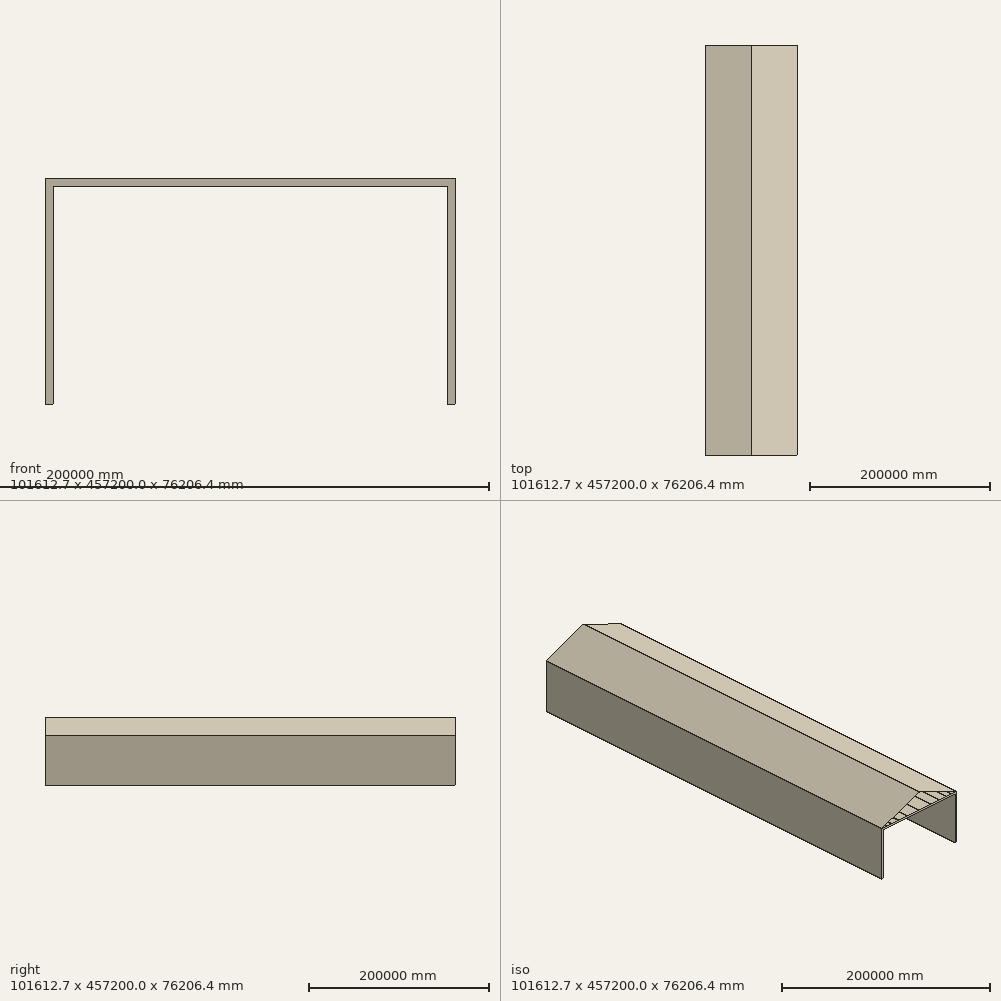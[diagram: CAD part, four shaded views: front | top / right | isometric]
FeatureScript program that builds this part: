
annotation { "Feature Type Name" : "Feature", "Feature Type Description" : "" }
export const myFeature = defineFeature(function(context is Context, id is Id, definition is map)
    precondition{}
    {
        {
            var Q0;
            Q0=qCreatedBy(makeId("Front.planeOp"),FACE);
            var sketch = newSketch(context, id + "F0", { "sketchPlane" : qUnion([Q0])});
            skLineSegment(sketch, "E0.bottom", {"start": v(0, 0) * mm, "end": v(2032, 0) * mm});
            skLineSegment(sketch, "E0.top", {"start": v(0, 55880) * mm, "end": v(101600, 55880) * mm});
            skLineSegment(sketch, "E0.left", {"start": v(0, 0) * mm, "end": v(0, 55880) * mm});
            skLineSegment(sketch, "E0.right", {"start": v(101600, 0) * mm, "end": v(101600, 55880) * mm});
            skLineSegment(sketch, "E1", {"start": v(0, 55880) * mm, "end": v(50800, 76200) * mm});
            skLineSegment(sketch, "E2", {"start": v(50800, 76200) * mm, "end": v(101600, 55880) * mm});
            skLineSegment(sketch, "E3.0", {"start": v(99568, 0) * mm, "end": v(99568, 53848) * mm});
            skLineSegment(sketch, "E3.1", {"start": v(2032, 53848) * mm, "end": v(99568, 53848) * mm});
            skLineSegment(sketch, "E3.2", {"start": v(2032, 0) * mm, "end": v(2032, 53848) * mm});
            skLineSegment(sketch, "E4.trimOffspring", {"start": v(99568, 0) * mm, "end": v(101600, 0) * mm});
            skLineSegment(sketch, "E5", {"start": v(50800, 76200) * mm, "end": v(50800, 55880) * mm});
            skLineSegment(sketch, "E6", {"start": v(50800, 55880) * mm, "end": v(66873.13, 69770.75) * mm});
            skLineSegment(sketch, "E7", {"start": v(66873.13, 69770.75) * mm, "end": v(66873.13, 55880) * mm});
            skLineSegment(sketch, "E8", {"start": v(66873.13, 55880) * mm, "end": v(77924.53, 65343.35) * mm});
            skLineSegment(sketch, "E9", {"start": v(77924.53, 65343.35) * mm, "end": v(78532.68, 55880) * mm});
            skLineSegment(sketch, "E10", {"start": v(78532.68, 55880) * mm, "end": v(88076.68, 61289.33) * mm});
            skLineSegment(sketch, "E11", {"start": v(88076.68, 61289.33) * mm, "end": v(88076.68, 55880) * mm});
            skLineSegment(sketch, "E12", {"start": v(88076.68, 55880) * mm, "end": v(94838.34, 58584.66) * mm});
            skLineSegment(sketch, "E13", {"start": v(94838.34, 58584.66) * mm, "end": v(94838.34, 55880) * mm});
            skLineSegment(sketch, "E14.MirrorCS", {"start": v(50800, 55880) * mm, "end": v(34726.87, 69770.75) * mm});
            skLineSegment(sketch, "E15.MirrorCS", {"start": v(34726.87, 69770.75) * mm, "end": v(34726.87, 55880) * mm});
            skLineSegment(sketch, "E16.MirrorCS", {"start": v(34726.87, 55880) * mm, "end": v(23675.47, 65343.35) * mm});
            skLineSegment(sketch, "E17.MirrorCS", {"start": v(23675.47, 65343.35) * mm, "end": v(23067.32, 55880) * mm});
            skLineSegment(sketch, "E18.MirrorCS", {"start": v(23067.32, 55880) * mm, "end": v(13523.32, 61289.33) * mm});
            skLineSegment(sketch, "E19.MirrorCS", {"start": v(13523.32, 61289.33) * mm, "end": v(13523.32, 55880) * mm});
            skLineSegment(sketch, "E20.MirrorCS", {"start": v(13523.32, 55880) * mm, "end": v(6761.66, 58584.66) * mm});
            skLineSegment(sketch, "E21.MirrorCS", {"start": v(6761.66, 58584.66) * mm, "end": v(6761.66, 55880) * mm});
            skArc(sketch, "E22.0.startCap", {"start": v(2.36, 55874.1) * mm, "mid": v(-5.9, 55877.64) * mm, "end": v(-2.36, 55885.9) * mm});
            skArc(sketch, "E22.0.endCap", {"start": v(50797.64, 76205.9) * mm, "mid": v(50805.9, 76202.36) * mm, "end": v(50802.36, 76194.1) * mm});
            skLineSegment(sketch, "E22.0.left", {"start": v(-2.36, 55885.9) * mm, "end": v(50797.64, 76205.9) * mm});
            skLineSegment(sketch, "E22.0.right", {"start": v(2.36, 55874.1) * mm, "end": v(50802.36, 76194.1) * mm});
            skArc(sketch, "E22.1.startCap", {"start": v(50793.65, 76200) * mm, "mid": v(50800, 76206.35) * mm, "end": v(50806.35, 76200) * mm});
            skArc(sketch, "E22.1.endCap", {"start": v(50806.35, 55880) * mm, "mid": v(50800, 55873.65) * mm, "end": v(50793.65, 55880) * mm});
            skLineSegment(sketch, "E22.1.left", {"start": v(50806.35, 76200) * mm, "end": v(50806.35, 55880) * mm});
            skLineSegment(sketch, "E22.1.right", {"start": v(50793.65, 76200) * mm, "end": v(50793.65, 55880) * mm});
            skArc(sketch, "E22.2.startCap", {"start": v(50804.15, 55884.8) * mm, "mid": v(50804.8, 55875.85) * mm, "end": v(50795.85, 55875.2) * mm});
            skArc(sketch, "E22.2.endCap", {"start": v(34722.72, 69765.94) * mm, "mid": v(34722.06, 69774.9) * mm, "end": v(34731.02, 69775.55) * mm});
            skLineSegment(sketch, "E22.2.left", {"start": v(50795.85, 55875.2) * mm, "end": v(34722.72, 69765.94) * mm});
            skLineSegment(sketch, "E22.2.right", {"start": v(50804.15, 55884.8) * mm, "end": v(34731.02, 69775.55) * mm});
            skArc(sketch, "E22.3.startCap", {"start": v(34720.52, 69770.75) * mm, "mid": v(34726.87, 69777.1) * mm, "end": v(34733.22, 69770.75) * mm});
            skArc(sketch, "E22.3.endCap", {"start": v(34733.22, 55880) * mm, "mid": v(34726.87, 55873.65) * mm, "end": v(34720.52, 55880) * mm});
            skLineSegment(sketch, "E22.3.left", {"start": v(34733.22, 69770.75) * mm, "end": v(34733.22, 55880) * mm});
            skLineSegment(sketch, "E22.3.right", {"start": v(34720.52, 69770.75) * mm, "end": v(34720.52, 55880) * mm});
            skArc(sketch, "E22.4.startCap", {"start": v(34731, 55884.82) * mm, "mid": v(34731.7, 55875.87) * mm, "end": v(34722.74, 55875.18) * mm});
            skArc(sketch, "E22.4.endCap", {"start": v(23671.34, 65338.53) * mm, "mid": v(23670.65, 65347.48) * mm, "end": v(23679.6, 65348.17) * mm});
            skLineSegment(sketch, "E22.4.left", {"start": v(34722.74, 55875.18) * mm, "end": v(23671.34, 65338.53) * mm});
            skLineSegment(sketch, "E22.4.right", {"start": v(34731, 55884.82) * mm, "end": v(23679.6, 65348.17) * mm});
            skArc(sketch, "E22.5.startCap", {"start": v(23669.13, 65343.76) * mm, "mid": v(23675.88, 65349.69) * mm, "end": v(23681.8, 65342.94) * mm});
            skArc(sketch, "E22.5.endCap", {"start": v(23073.66, 55879.6) * mm, "mid": v(23066.92, 55873.66) * mm, "end": v(23060.99, 55880.4) * mm});
            skLineSegment(sketch, "E22.5.left", {"start": v(23681.8, 65342.94) * mm, "end": v(23073.66, 55879.6) * mm});
            skLineSegment(sketch, "E22.5.right", {"start": v(23669.13, 65343.76) * mm, "end": v(23060.99, 55880.4) * mm});
            skArc(sketch, "E22.6.startCap", {"start": v(23070.45, 55885.52) * mm, "mid": v(23072.85, 55876.87) * mm, "end": v(23064.2, 55874.48) * mm});
            skArc(sketch, "E22.6.endCap", {"start": v(13520.2, 61283.8) * mm, "mid": v(13517.8, 61292.46) * mm, "end": v(13526.45, 61294.85) * mm});
            skLineSegment(sketch, "E22.6.left", {"start": v(23064.2, 55874.48) * mm, "end": v(13520.2, 61283.8) * mm});
            skLineSegment(sketch, "E22.6.right", {"start": v(23070.45, 55885.52) * mm, "end": v(13526.45, 61294.85) * mm});
            skArc(sketch, "E22.7.startCap", {"start": v(13516.97, 61289.33) * mm, "mid": v(13523.32, 61295.68) * mm, "end": v(13529.67, 61289.33) * mm});
            skArc(sketch, "E22.7.endCap", {"start": v(13529.67, 55880) * mm, "mid": v(13523.32, 55873.65) * mm, "end": v(13516.97, 55880) * mm});
            skLineSegment(sketch, "E22.7.left", {"start": v(13529.67, 61289.33) * mm, "end": v(13529.67, 55880) * mm});
            skLineSegment(sketch, "E22.7.right", {"start": v(13516.97, 61289.33) * mm, "end": v(13516.97, 55880) * mm});
            skArc(sketch, "E22.8.startCap", {"start": v(13525.68, 55885.9) * mm, "mid": v(13529.22, 55877.64) * mm, "end": v(13520.96, 55874.1) * mm});
            skArc(sketch, "E22.8.endCap", {"start": v(6759.3, 58578.77) * mm, "mid": v(6755.77, 58587.02) * mm, "end": v(6764.02, 58590.56) * mm});
            skLineSegment(sketch, "E22.8.left", {"start": v(13520.96, 55874.1) * mm, "end": v(6759.3, 58578.77) * mm});
            skLineSegment(sketch, "E22.8.right", {"start": v(13525.68, 55885.9) * mm, "end": v(6764.02, 58590.56) * mm});
            skArc(sketch, "E22.9.startCap", {"start": v(6755.31, 58584.66) * mm, "mid": v(6761.66, 58591.01) * mm, "end": v(6768.01, 58584.66) * mm});
            skArc(sketch, "E22.9.endCap", {"start": v(6768.01, 55880) * mm, "mid": v(6761.66, 55873.65) * mm, "end": v(6755.31, 55880) * mm});
            skLineSegment(sketch, "E22.9.left", {"start": v(6768.01, 58584.66) * mm, "end": v(6768.01, 55880) * mm});
            skLineSegment(sketch, "E22.9.right", {"start": v(6755.31, 58584.66) * mm, "end": v(6755.31, 55880) * mm});
            skArc(sketch, "E22.10.startCap", {"start": v(50804.15, 55875.2) * mm, "mid": v(50795.2, 55875.85) * mm, "end": v(50795.85, 55884.8) * mm});
            skArc(sketch, "E22.10.endCap", {"start": v(66868.98, 69775.55) * mm, "mid": v(66877.94, 69774.9) * mm, "end": v(66877.28, 69765.94) * mm});
            skLineSegment(sketch, "E22.10.left", {"start": v(50795.85, 55884.8) * mm, "end": v(66868.98, 69775.55) * mm});
            skLineSegment(sketch, "E22.10.right", {"start": v(50804.15, 55875.2) * mm, "end": v(66877.28, 69765.94) * mm});
            skArc(sketch, "E22.11.startCap", {"start": v(50797.64, 76194.1) * mm, "mid": v(50794.1, 76202.36) * mm, "end": v(50802.36, 76205.9) * mm});
            skArc(sketch, "E22.11.endCap", {"start": v(101602.36, 55885.9) * mm, "mid": v(101605.9, 55877.64) * mm, "end": v(101597.64, 55874.1) * mm});
            skLineSegment(sketch, "E22.11.left", {"start": v(50802.36, 76205.9) * mm, "end": v(101602.36, 55885.9) * mm});
            skLineSegment(sketch, "E22.11.right", {"start": v(50797.64, 76194.1) * mm, "end": v(101597.64, 55874.1) * mm});
            skArc(sketch, "E22.12.startCap", {"start": v(66866.78, 69770.75) * mm, "mid": v(66873.13, 69777.1) * mm, "end": v(66879.48, 69770.75) * mm});
            skArc(sketch, "E22.12.endCap", {"start": v(66879.48, 55880) * mm, "mid": v(66873.13, 55873.65) * mm, "end": v(66866.78, 55880) * mm});
            skLineSegment(sketch, "E22.12.left", {"start": v(66879.48, 69770.75) * mm, "end": v(66879.48, 55880) * mm});
            skLineSegment(sketch, "E22.12.right", {"start": v(66866.78, 69770.75) * mm, "end": v(66866.78, 55880) * mm});
            skArc(sketch, "E22.13.startCap", {"start": v(66877.26, 55875.18) * mm, "mid": v(66868.3, 55875.87) * mm, "end": v(66869, 55884.82) * mm});
            skArc(sketch, "E22.13.endCap", {"start": v(77920.4, 65348.17) * mm, "mid": v(77929.35, 65347.48) * mm, "end": v(77928.66, 65338.53) * mm});
            skLineSegment(sketch, "E22.13.left", {"start": v(66869, 55884.82) * mm, "end": v(77920.4, 65348.17) * mm});
            skLineSegment(sketch, "E22.13.right", {"start": v(66877.26, 55875.18) * mm, "end": v(77928.66, 65338.53) * mm});
            skArc(sketch, "E22.14.startCap", {"start": v(77918.2, 65342.94) * mm, "mid": v(77924.12, 65349.69) * mm, "end": v(77930.87, 65343.76) * mm});
            skArc(sketch, "E22.14.endCap", {"start": v(78539.01, 55880.4) * mm, "mid": v(78533.08, 55873.66) * mm, "end": v(78526.34, 55879.6) * mm});
            skLineSegment(sketch, "E22.14.left", {"start": v(77930.87, 65343.76) * mm, "end": v(78539.01, 55880.4) * mm});
            skLineSegment(sketch, "E22.14.right", {"start": v(77918.2, 65342.94) * mm, "end": v(78526.34, 55879.6) * mm});
            skArc(sketch, "E22.15.startCap", {"start": v(78535.8, 55874.48) * mm, "mid": v(78527.15, 55876.87) * mm, "end": v(78529.55, 55885.52) * mm});
            skArc(sketch, "E22.15.endCap", {"start": v(88073.55, 61294.85) * mm, "mid": v(88082.2, 61292.46) * mm, "end": v(88079.8, 61283.8) * mm});
            skLineSegment(sketch, "E22.15.left", {"start": v(78529.55, 55885.52) * mm, "end": v(88073.55, 61294.85) * mm});
            skLineSegment(sketch, "E22.15.right", {"start": v(78535.8, 55874.48) * mm, "end": v(88079.8, 61283.8) * mm});
            skArc(sketch, "E22.16.startCap", {"start": v(88070.33, 61289.33) * mm, "mid": v(88076.68, 61295.68) * mm, "end": v(88083.03, 61289.33) * mm});
            skArc(sketch, "E22.16.endCap", {"start": v(88083.03, 55880) * mm, "mid": v(88076.68, 55873.65) * mm, "end": v(88070.33, 55880) * mm});
            skLineSegment(sketch, "E22.16.left", {"start": v(88083.03, 61289.33) * mm, "end": v(88083.03, 55880) * mm});
            skLineSegment(sketch, "E22.16.right", {"start": v(88070.33, 61289.33) * mm, "end": v(88070.33, 55880) * mm});
            skArc(sketch, "E22.17.startCap", {"start": v(94831.99, 58584.66) * mm, "mid": v(94838.34, 58591.01) * mm, "end": v(94844.69, 58584.66) * mm});
            skArc(sketch, "E22.17.endCap", {"start": v(94844.69, 55880) * mm, "mid": v(94838.34, 55873.65) * mm, "end": v(94831.99, 55880) * mm});
            skLineSegment(sketch, "E22.17.left", {"start": v(94844.69, 58584.66) * mm, "end": v(94844.69, 55880) * mm});
            skLineSegment(sketch, "E22.17.right", {"start": v(94831.99, 58584.66) * mm, "end": v(94831.99, 55880) * mm});
            skArc(sketch, "E22.18.startCap", {"start": v(88079.04, 55874.1) * mm, "mid": v(88070.78, 55877.64) * mm, "end": v(88074.32, 55885.9) * mm});
            skArc(sketch, "E22.18.endCap", {"start": v(94835.98, 58590.56) * mm, "mid": v(94844.23, 58587.02) * mm, "end": v(94840.7, 58578.77) * mm});
            skLineSegment(sketch, "E22.18.left", {"start": v(88074.32, 55885.9) * mm, "end": v(94835.98, 58590.56) * mm});
            skLineSegment(sketch, "E22.18.right", {"start": v(88079.04, 55874.1) * mm, "end": v(94840.7, 58578.77) * mm});
            skSolve(sketch);
        }
        {
            var Q0;
            Q0 = qSketchRegion(id + "F0", true);
            extrude(context, id + "F1", {"entities" : qUnion([Q0]), "depth" : 457200 * mm, "offsetDistance" : 25.4 * mm});
        }
    });
